# Revit family: Haworth_Archibald_Seating
name_source: partatom
category: Furniture
revit_build: Autodesk Revit 2018 (Build: 20170223_1515(x64)
units: mm (PartAtom-declared; Revit-internal decimal feet)

## family parameters
Always vertical = Yes
Cut with Voids When Loaded = No
OmniClass Number = 23.40.20.00
OmniClass Title = General Furniture and Specialties
Room Calculation Point = No
Shared = No
Work Plane-Based = No

## types (3) — shared parameters
Actual Depth = 3' - 0"
Actual Height = 3' - 7"
Actual Width = 2' - 8"
Assembly Code = E2020200
Description = Haworth Archibald Seating
Frame Finish = Haworth _ Paint _ Metallic Gunmetal
Manufacturer = Haworth
Model = HCPF-ARL1
Size = Verify Final Dim. w/ Haworth
URL = http://www.haworth.com
URL - Product = http://www.haworth.com
Version = 4
Warranty = http://www.haworth.com

## per-type parameters (varying)
| type | Armchair | High Back Actual | Highback | King Headrest |
| HCPF-ARL1-H - Highback | No | Yes | Yes | No |
| HCPF-ARL1-S - Armchair | Yes | No | No | No |
| HCPF-ARL1-K - King Headrest | No | Yes | No | Yes |

## geometry (parser evidence)
native form markers: Sweep x2
no freeform markers — native parametric forms only
